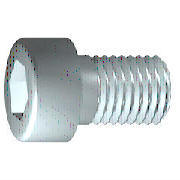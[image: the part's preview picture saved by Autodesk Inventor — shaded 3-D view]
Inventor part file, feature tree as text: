
AUTODESK INVENTOR PART (.ipt)
format: ipt  version: 2024.3 (Build 283343000, 343)  size: 190,976 bytes
history: native  units: mm (DEFAULTED — no unit token found)
features: extrude x1, plane x1, fillet x1
ambient origin geometry x7: Origin, YZ Plane, XY Plane, X Axis, Y Axis, Z Axis, Center Point
bodies: Solid1 (feature_tree), Body (feature_tree)
feature tree (3):
  extrude  "Slot"  Depth=22.5mm
  plane  "Work Plane1"
  fillet  "Fillet2"  Radius=0.61355mm
